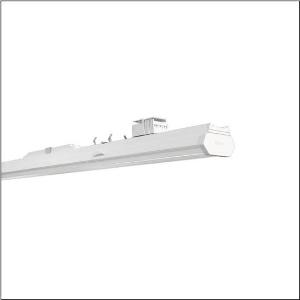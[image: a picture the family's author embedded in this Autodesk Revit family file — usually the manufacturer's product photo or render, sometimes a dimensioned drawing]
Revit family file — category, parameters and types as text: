
# Revit family: licross_r__11_protected_mo_51td11dn495g_7274
name_source: partatom
category: Lighting Fixtures
units: mm (PartAtom-declared; Revit-internal decimal feet)

## family parameters
Cut with Voids When Loaded = No
Host = Face
Light Source = No
Part Type = Normal
Room Calculation Point = No
Round Connector Dimension = Use Diameter
Shared = No

## types (1)
- --- (1 x LED, 9930 lm, 57.1 W, 4000K)
    Apparent Load = 57 VA
    CIE Flux Codes = 83 94 98 100 100
    Color Rendering = 80
    Color Temperature = 4000K
    Default Elevation = 1800 mm
    Description = Licross® 11 Protected MO, luminaire insert, of sheet steel, galvanised, coil coated, white, length: 1.500mm, width: 90mm, height: 101mm, LED rated luminous flux: 9.930lm, light colour: 840, control gear: DALI 2, with plug, 5-pole, with phase selection, mains connection: 220..240V, AC, 50/60Hz, rated input power: 57W, halogen-free wiring, primary light control with lens, of plastic, primary optical cover: cover, of PMMA, light emission: direct distribution, primary light characteristic: symmetric, protection rating (complete): IP54, insulation class (complete): insulation class I (protective earthing), certification: CE, ENEC, VDE, UKCA, protection symbol: D if used in an environment with non-conductive dust loads with corresponding accessories, impact resistance: IK06, permissible ambient temperature for indoor applications: -25..+35°C, corresponds to IFS (International Featured Standards) requirements for safety and quality in the food industry, reducing of maximum allowable ambient temperature of 5°C with ceiling mounting, LABS conformity tested according to VDMA 24364:2018-05, packaging unit: 1 piece
    Height = 92 mm
    Lamp = 1 x LED
    Lamp Light Flux = 9930 lm
    Lamp Power = 57.1 W
    Lamp count = 1
    Length = 1500 mm
    Luminous efficacy = 174 lm/W
    Manufacturer = Siteco
    ModVariant = No
    Model = 51TD11DN495G
    Mounting Place = Ceiling
    Mounting Type = Pendant
    Number of Poles = 1
    OnlyDefault = Yes
    Power Factor = 1
    Product Name = Licross® 11 Protected MO
    Product group = luminaire insert
    ProductGroupID = 901
    Protection Class = Protection class I
    Protection Degree = IP 54
    RLX_Detail_Level = 1
    RLX_Emergency_Light_Flux = 0 lm
    RLX_Emergency_Type = 0
    RLX_Emergency_Type_DB = No
    RlxData = <blob elided: 24161 chars, md5=d5d1b738>
    Socket = socket
    Standby Power = 0 W
    System Light Flux = 9930 lm
    System Power = 57 W
    Type Comments = factory setting: luminous flux: 100 % | dim-lin: 254 | 378 mA
    Type Image = l_1256145.jpg
    URL = http://relux.com
    VarID = @adj_031099
    Voltage = 0 V
    Weight = 0.00 kg
    Width = 88 mm

## geometry (parser evidence)
native form markers: Blend x4, Sweep x10
no freeform markers — native parametric forms only
